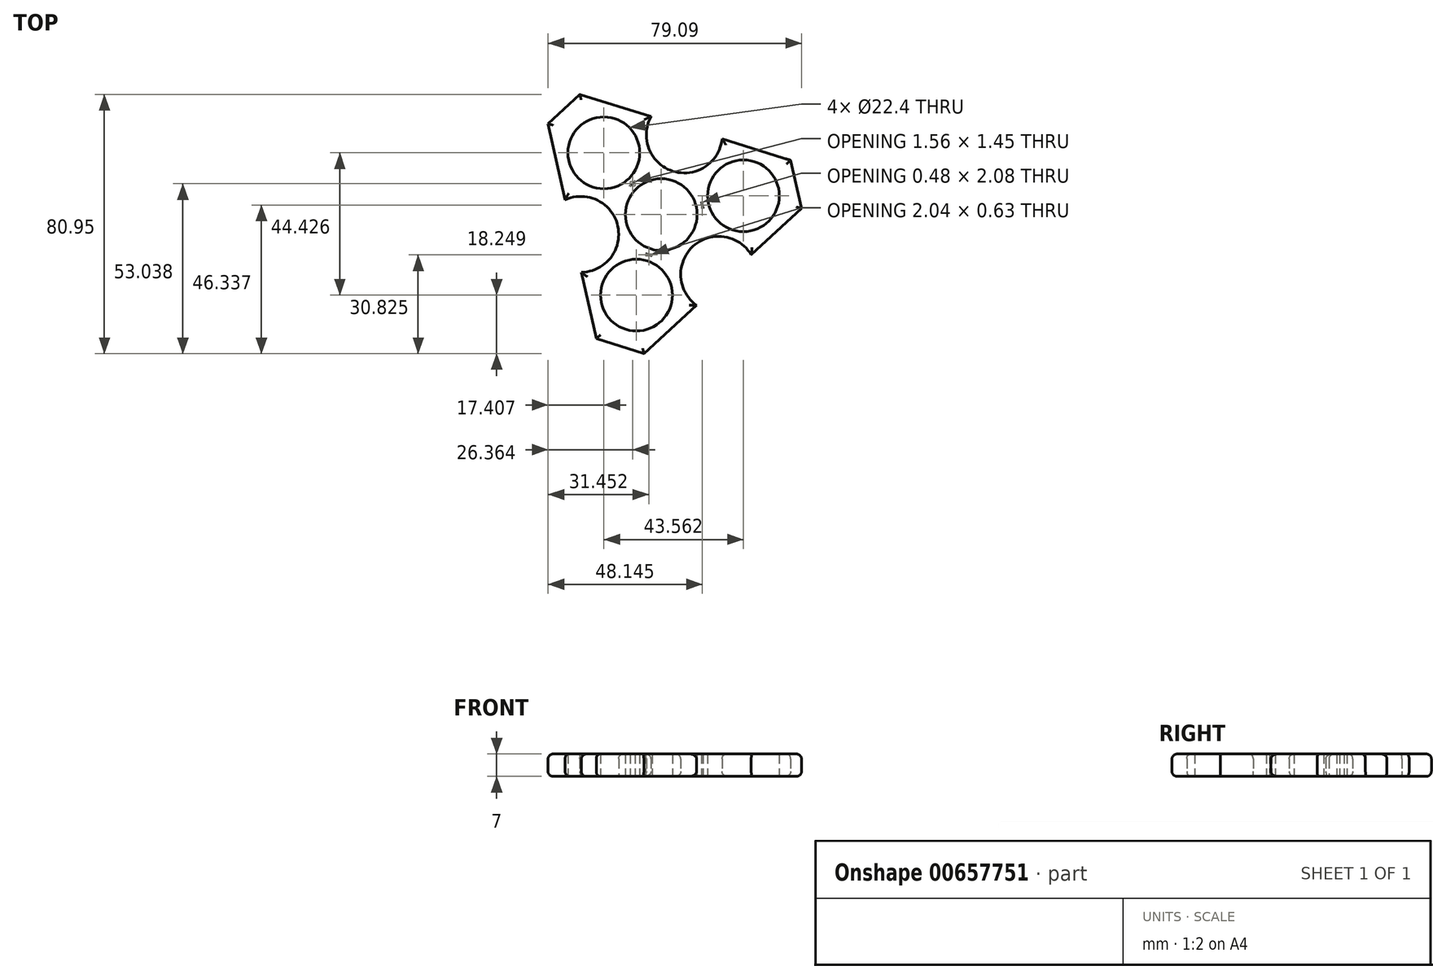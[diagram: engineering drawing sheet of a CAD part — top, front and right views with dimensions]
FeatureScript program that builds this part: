
annotation { "Feature Type Name" : "Feature", "Feature Type Description" : "" }
export const myFeature = defineFeature(function(context is Context, id is Id, definition is map)
    precondition{}
    {
        {
            var Q0;
            Q0=qCreatedBy(makeId("Top.planeOp"),FACE);
            var sketch = newSketch(context, id + "F0", { "sketchPlane" : qUnion([Q0])});
            skLineSegment(sketch, "E0.0", {"start": v(43.77, 1.89) * mm, "end": v(28.08, -12.56) * mm});
            skLineSegment(sketch, "E0.1", {"start": v(-20.27, -38.76) * mm, "end": v(-24.91, -18.04) * mm});
            skLineSegment(sketch, "E0.2", {"start": v(-25.38, 37.55) * mm, "end": v(-3.17, 30.6) * mm});
            skPoint(sketch, "E0.0.midPoint", {"position": v(19.14, -20.79) * mm});
            skCircle(sketch, "E1", {"center": v(0, 0) * mm, "radius": 11.2 * mm});
            skArc(sketch, "E2", {"start": v(-8.17, 10.36) * mm, "mid": v(-8.99, 9.67) * mm, "end": v(-9.74, 8.91) * mm});
            skCircle(sketch, "E3", {"center": v(-17.91, 19.28) * mm, "radius": 11.2 * mm});
            skArc(sketch, "E4", {"start": v(-9.74, 8.91) * mm, "mid": v(-8.93, 9.6) * mm, "end": v(-8.17, 10.36) * mm});
            skArc(sketch, "E5.1.0", {"start": v(-2.85, -12.89) * mm, "mid": v(-3.86, -12.53) * mm, "end": v(-4.89, -12.26) * mm});
            skCircle(sketch, "E5.1.1", {"center": v(-7.74, -25.15) * mm, "radius": 11.2 * mm});
            skArc(sketch, "E5.2.0", {"start": v(12.59, 3.98) * mm, "mid": v(12.78, 2.93) * mm, "end": v(13.06, 1.9) * mm});
            skCircle(sketch, "E5.2.1", {"center": v(25.65, 5.87) * mm, "radius": 11.2 * mm});
            skLineSegment(sketch, "E6.5", {"start": v(-20.27, -38.76) * mm, "end": v(-5.43, -43.4) * mm});
            skPoint(sketch, "E6.0.midPoint", {"position": v(-3.73, -50.99) * mm});
            skLineSegment(sketch, "E7.3", {"start": v(43.77, 1.89) * mm, "end": v(40.4, 16.97) * mm});
            skPoint(sketch, "E7.0.midPoint", {"position": v(68.2, 15.28) * mm});
            skLineSegment(sketch, "E8.3", {"start": v(-25.38, 37.55) * mm, "end": v(-35.32, 28.4) * mm});
            skPoint(sketch, "E8.0.midPoint", {"position": v(-46.2, 50.18) * mm});
            skPoint(sketch, "E9.orphan", {"position": v(-51.17, 45.61) * mm});
            skPoint(sketch, "E8.1.start.orphan", {"position": v(-41.23, 54.76) * mm});
            skPoint(sketch, "E10.orphan", {"position": v(-2.03, -58.58) * mm});
            skPoint(sketch, "E6.cCircle.center.orphan", {"position": v(-16.87, -53.93) * mm});
            skPoint(sketch, "E11.orphan", {"position": v(58.52, -2.73) * mm});
            skPoint(sketch, "E7.cCircle.center.orphan", {"position": v(55.14, 12.36) * mm});
            skPoint(sketch, "E12.orphan", {"position": v(69.9, 7.74) * mm});
            skPoint(sketch, "E7.5.end.orphan", {"position": v(66.52, 22.83) * mm});
            skArc(sketch, "E13", {"start": v(-24.91, -18.04) * mm, "mid": v(-13.56, -3.6) * mm, "end": v(-30, 4.63) * mm});
            skArc(sketch, "E14.1.0", {"start": v(28.08, -12.56) * mm, "mid": v(9.9, -9.95) * mm, "end": v(10.99, -28.29) * mm});
            skArc(sketch, "E14.2.0", {"start": v(-3.17, 30.6) * mm, "mid": v(3.67, 13.54) * mm, "end": v(19, 23.66) * mm});
            skLineSegment(sketch, "E15.trimOffspring", {"start": v(-30, 4.63) * mm, "end": v(-35.32, 28.4) * mm});
            skLineSegment(sketch, "E16.trimOffspring", {"start": v(19, 23.66) * mm, "end": v(40.4, 16.97) * mm});
            skLineSegment(sketch, "E17.trimOffspring", {"start": v(10.99, -28.29) * mm, "end": v(-5.43, -43.4) * mm});
            skArc(sketch, "E18.trimOffspring", {"start": v(13.06, 1.9) * mm, "mid": v(12.87, 2.95) * mm, "end": v(12.59, 3.98) * mm});
            skArc(sketch, "E19.trimOffspring", {"start": v(-4.89, -12.26) * mm, "mid": v(-3.88, -12.62) * mm, "end": v(-2.85, -12.89) * mm});
            skSolve(sketch);
        }
        {
            var Q0;
            Q0=makeQuery(id+"F0.imprint","IMPRINT",FACE,{"disambiguationData":[TD([[makeQuery(id+"F0.imprint","IMPRINT",EDGE,{"derivedFrom":sQuery(id+"F0.wireOp",EDGE,"E0.0")}),-1.0]])]});
            extrude(context, id + "F1", {"entities" : qUnion([Q0]), "depth" : 7 * mm, "offsetDistance" : 25 * mm});
        }
        {
            var Q0;
            Q0=makeQuery(id+"F1.opExtrude","CAP_EDGE",EDGE,{"disambiguationData":[OSD([sQuery(id+"F0.wireOp",EDGE,"E6.5")])],"isStart":false});
            var Q1;
            Q1=makeQuery(id+"F1.opExtrude","CAP_EDGE",EDGE,{"disambiguationData":[OSD([sQuery(id+"F0.wireOp",EDGE,"E17.trimOffspring")])],"isStart":false});
            var Q2;
            Q2=makeQuery(id+"F1.opExtrude","CAP_EDGE",EDGE,{"disambiguationData":[OSD([sQuery(id+"F0.wireOp",EDGE,"E14.1.0")])],"isStart":false});
            var Q3;
            Q3=makeQuery(id+"F1.opExtrude","CAP_EDGE",EDGE,{"disambiguationData":[OSD([sQuery(id+"F0.wireOp",EDGE,"E0.0")])],"isStart":false});
            var Q4;
            Q4=makeQuery(id+"F1.opExtrude","CAP_EDGE",EDGE,{"disambiguationData":[OSD([sQuery(id+"F0.wireOp",EDGE,"E7.3")])],"isStart":false});
            var Q5;
            Q5=makeQuery(id+"F1.opExtrude","CAP_EDGE",EDGE,{"disambiguationData":[OSD([sQuery(id+"F0.wireOp",EDGE,"E16.trimOffspring")])],"isStart":false});
            var Q6;
            Q6=makeQuery(id+"F1.opExtrude","CAP_EDGE",EDGE,{"disambiguationData":[OSD([sQuery(id+"F0.wireOp",EDGE,"E14.2.0")])],"isStart":false});
            var Q7;
            Q7=makeQuery(id+"F1.opExtrude","CAP_EDGE",EDGE,{"disambiguationData":[OSD([sQuery(id+"F0.wireOp",EDGE,"E13")])],"isStart":false});
            var Q8;
            Q8=makeQuery(id+"F1.opExtrude","CAP_EDGE",EDGE,{"disambiguationData":[OSD([sQuery(id+"F0.wireOp",EDGE,"E0.1")])],"isStart":false});
            var Q9;
            Q9=makeQuery(id+"F1.opExtrude","CAP_EDGE",EDGE,{"disambiguationData":[OSD([sQuery(id+"F0.wireOp",EDGE,"E15.trimOffspring")])],"isStart":false});
            var Q10;
            Q10=makeQuery(id+"F1.opExtrude","CAP_EDGE",EDGE,{"disambiguationData":[OSD([sQuery(id+"F0.wireOp",EDGE,"E0.2")])],"isStart":false});
            var Q11;
            Q11=makeQuery(id+"F1.opExtrude","CAP_EDGE",EDGE,{"disambiguationData":[OSD([sQuery(id+"F0.wireOp",EDGE,"E8.3")])],"isStart":false});
            fillet(context, id + "F2", {"entities" : qUnion([Q0, Q1, Q2, Q3, Q4, Q5, Q6, Q7, Q8, Q9, Q10, Q11]), "radius" : 1.5 * mm, "tangentPropagation" : true, "allowEdgeOverflow" : false});
        }
        {
            var Q0;
            Q0=makeQuery(id+"F1.opExtrude","CAP_EDGE",EDGE,{"disambiguationData":[OSD([sQuery(id+"F0.wireOp",EDGE,"E6.5")])],"isStart":true});
            var Q1;
            Q1=makeQuery(id+"F1.opExtrude","CAP_EDGE",EDGE,{"disambiguationData":[OSD([sQuery(id+"F0.wireOp",EDGE,"E0.1")])],"isStart":true});
            var Q2;
            Q2=makeQuery(id+"F1.opExtrude","CAP_EDGE",EDGE,{"disambiguationData":[OSD([sQuery(id+"F0.wireOp",EDGE,"E17.trimOffspring")])],"isStart":true});
            var Q3;
            {var subQ0=sQuery(id+"F0.wireOp",EDGE,"E16.trimOffspring");Q3=makeQuery(id+"F2.opFillet","BLEND_EDGE",EDGE,{"blendedFrom":[makeQuery(id+"F1.opExtrude","CAP_EDGE",EDGE,{"disambiguationData":[OSD([subQ0])],"isStart":false}),makeQuery(id+"F1.opExtrude","SWEPT_FACE",FACE,{"disambiguationData":[OSD([subQ0])]})],"blendedInto":[makeQuery(id+"F1.opExtrude","SWEPT_FACE",FACE,{"disambiguationData":[OSD([subQ0])]})]});}
            var Q4;
            Q4=makeQuery(id+"F1.opExtrude","CAP_EDGE",EDGE,{"disambiguationData":[OSD([sQuery(id+"F0.wireOp",EDGE,"E7.3")])],"isStart":true});
            var Q5;
            Q5=makeQuery(id+"F1.opExtrude","CAP_EDGE",EDGE,{"disambiguationData":[OSD([sQuery(id+"F0.wireOp",EDGE,"E0.0")])],"isStart":true});
            var Q6;
            Q6=makeQuery(id+"F1.opExtrude","CAP_EDGE",EDGE,{"disambiguationData":[OSD([sQuery(id+"F0.wireOp",EDGE,"E0.2")])],"isStart":true});
            var Q7;
            Q7=makeQuery(id+"F1.opExtrude","CAP_EDGE",EDGE,{"disambiguationData":[OSD([sQuery(id+"F0.wireOp",EDGE,"E8.3")])],"isStart":true});
            var Q8;
            Q8=makeQuery(id+"F1.opExtrude","CAP_EDGE",EDGE,{"disambiguationData":[OSD([sQuery(id+"F0.wireOp",EDGE,"E15.trimOffspring")])],"isStart":true});
            var Q9;
            {var subQ0=sQuery(id+"F0.wireOp",EDGE,"E13");Q9=makeQuery(id+"F2.opFillet","BLEND_EDGE",EDGE,{"blendedFrom":[makeQuery(id+"F1.opExtrude","CAP_EDGE",EDGE,{"disambiguationData":[OSD([subQ0])],"isStart":false}),makeQuery(id+"F1.opExtrude","SWEPT_FACE",FACE,{"disambiguationData":[OSD([subQ0])]})],"blendedInto":[makeQuery(id+"F1.opExtrude","SWEPT_FACE",FACE,{"disambiguationData":[OSD([subQ0])]})]});}
            var Q10;
            Q10=makeQuery(id+"F1.opExtrude","CAP_EDGE",EDGE,{"disambiguationData":[OSD([sQuery(id+"F0.wireOp",EDGE,"E14.1.0")])],"isStart":true});
            var Q11;
            Q11=makeQuery(id+"F1.opExtrude","CAP_EDGE",EDGE,{"disambiguationData":[OSD([sQuery(id+"F0.wireOp",EDGE,"E14.2.0")])],"isStart":true});
            fillet(context, id + "F3", {"entities" : qUnion([Q0, Q1, Q2, Q3, Q4, Q5, Q6, Q7, Q8, Q9, Q10, Q11]), "radius" : 1.5 * mm, "tangentPropagation" : true, "allowEdgeOverflow" : false});
        }
    });
